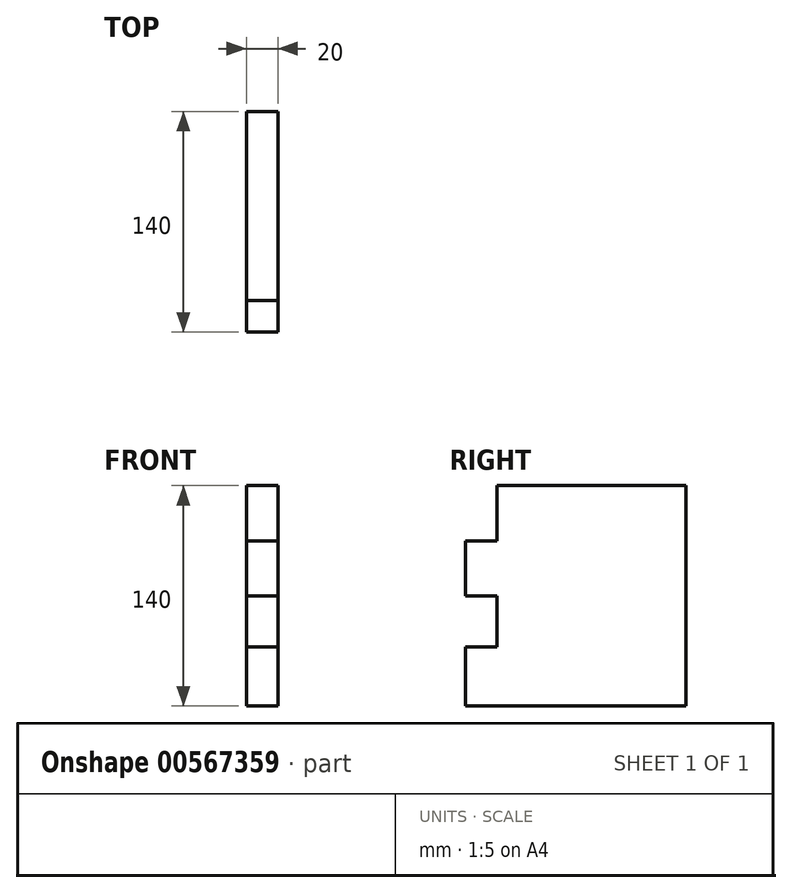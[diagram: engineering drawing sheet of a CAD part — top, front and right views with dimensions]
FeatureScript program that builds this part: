
annotation { "Feature Type Name" : "Feature", "Feature Type Description" : "" }
export const myFeature = defineFeature(function(context is Context, id is Id, definition is map)
    precondition{}
    {
        {
            var Q0;
            Q0=qCreatedBy(makeId("Right.planeOp"),FACE);
            var sketch = newSketch(context, id + "F0", { "sketchPlane" : qUnion([Q0])});
            skLineSegment(sketch, "E0.bottom", {"start": v(-128.86, 140) * mm, "end": v(-8.86, 140) * mm});
            skLineSegment(sketch, "E0.top", {"start": v(-148.86, 0) * mm, "end": v(-8.86, 0) * mm});
            skLineSegment(sketch, "E0.left", {"start": v(-148.86, 104.9) * mm, "end": v(-148.86, 70) * mm});
            skLineSegment(sketch, "E0.right", {"start": v(-8.86, 140) * mm, "end": v(-8.86, 0) * mm});
            skLineSegment(sketch, "E1.top", {"start": v(-148.86, 0) * mm, "end": v(-128.86, 0) * mm});
            skLineSegment(sketch, "E1.right", {"start": v(-128.86, 140) * mm, "end": v(-128.86, 104.9) * mm});
            skLineSegment(sketch, "E2.top", {"start": v(-148.86, 104.9) * mm, "end": v(-128.86, 104.9) * mm});
            skLineSegment(sketch, "E3.top", {"start": v(-148.86, 70) * mm, "end": v(-128.86, 70) * mm});
            skLineSegment(sketch, "E4.top", {"start": v(-148.86, 37.38) * mm, "end": v(-128.86, 37.38) * mm});
            skLineSegment(sketch, "E4.right", {"start": v(-128.86, 70) * mm, "end": v(-128.86, 37.38) * mm});
            skLineSegment(sketch, "E5.trimOffspring", {"start": v(-148.86, 37.38) * mm, "end": v(-148.86, 0) * mm});
            skSolve(sketch);
        }
        {
            var Q0;
            Q0 = qSketchRegion(id + "F0", true);
            extrude(context, id + "F1", {"entities" : qUnion([Q0]), "depth" : 20 * mm, "offsetDistance" : 25.4 * mm});
        }
    });
